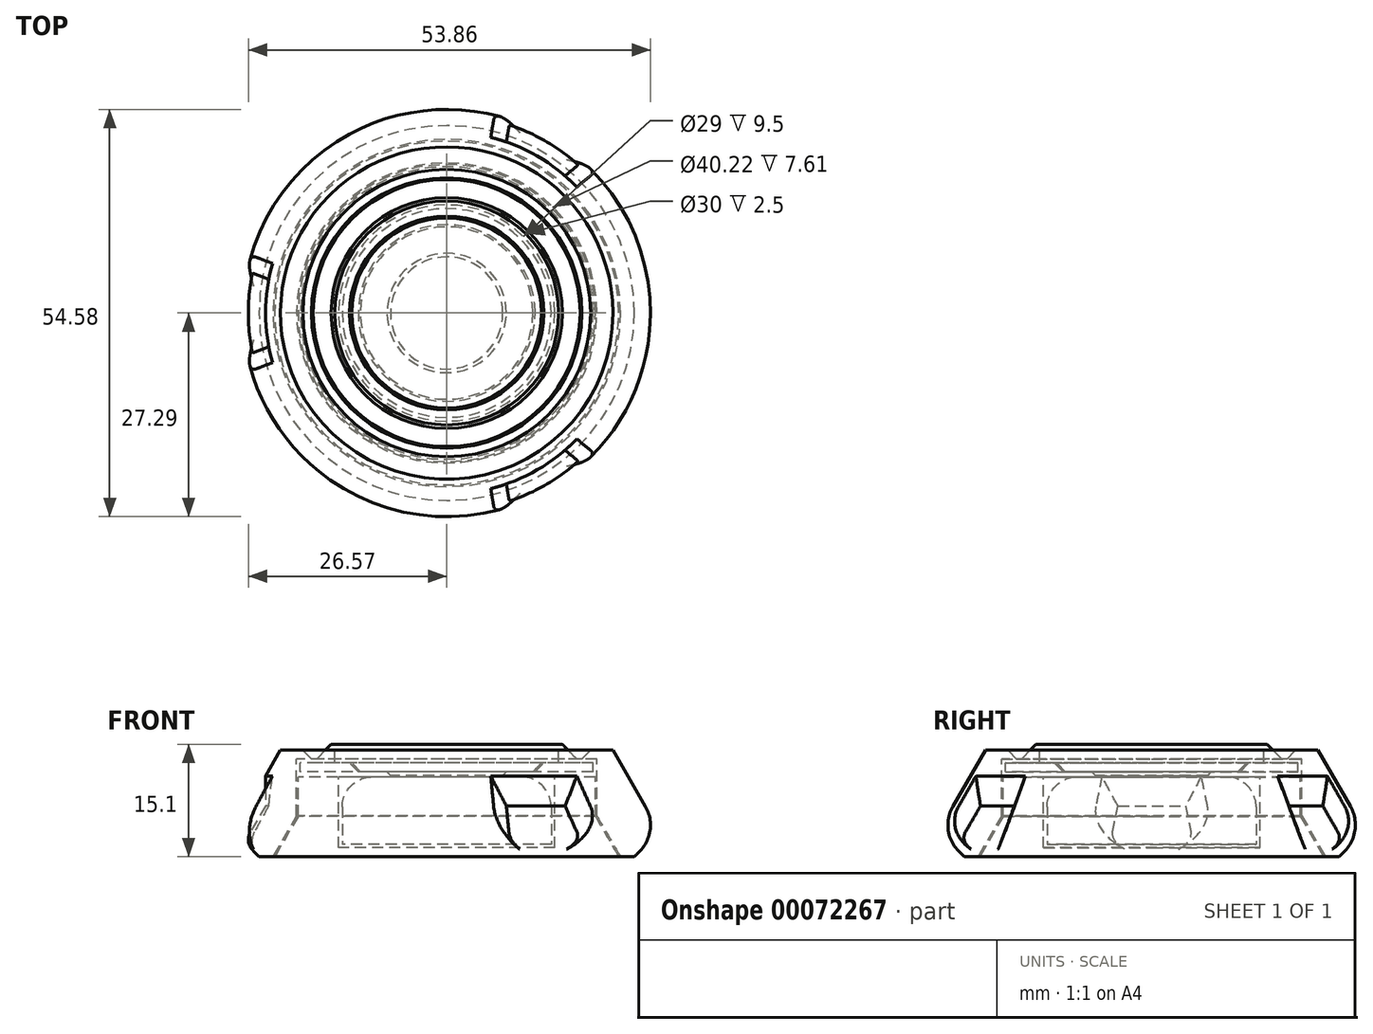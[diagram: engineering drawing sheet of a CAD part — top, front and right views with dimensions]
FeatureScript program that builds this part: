
annotation { "Feature Type Name" : "Feature", "Feature Type Description" : "" }
export const myFeature = defineFeature(function(context is Context, id is Id, definition is map)
    precondition{}
    {
        {
            var Q0;
            Q0=qCreatedBy(makeId("Top.planeOp"),FACE);
            var sketch = newSketch(context, id + "F0", { "sketchPlane" : qUnion([Q0])});
            skCircle(sketch, "E0", {"center": v(0, 0) * mm, "radius": 14 * mm});
            skSolve(sketch);
        }
        {
            var Q0;
            Q0=makeQuery(id+"F0.imprint","IMPRINT",FACE,{"disambiguationData":[TD([[makeQuery(id+"F0.imprint","IMPRINT",EDGE,{"derivedFrom":sQuery(id+"F0.wireOp",EDGE,"E0")}),1.0]])]});
            extrude(context, id + "F1", {"entities" : qUnion([Q0]), "depth" : 9 * mm});
        }
        {
            var Q0;
            Q0=makeQuery(id+"F1.opExtrude","CAP_EDGE",EDGE,{"disambiguationData":[OSD([sQuery(id+"F0.wireOp",EDGE,"E0")])],"isStart":false});
            fillet(context, id + "F2", {"entities" : qUnion([Q0]), "radius" : 4 * mm, "tangentPropagation" : true, "allowEdgeOverflow" : false});
        }
        {
            var Q0;
            Q0=qCreatedBy(makeId("Front.planeOp"),FACE);
            var sketch = newSketch(context, id + "F3", { "sketchPlane" : qUnion([Q0])});
            skLineSegment(sketch, "E1", {"start": v(-14.5, 9) * mm, "end": v(-14.5, -0.5) * mm});
            skLineSegment(sketch, "E2", {"start": v(-14.5, -0.5) * mm, "end": v(0, -0.5) * mm});
            skLineSegment(sketch, "E3", {"start": v(-14, 0) * mm, "end": v(-14, 5) * mm, "construction": true});
            skLineSegment(sketch, "E4", {"start": v(0, -0.5) * mm, "end": v(0, -1.7) * mm});
            skLineSegment(sketch, "E5", {"start": v(0, -1.7) * mm, "end": v(-23.05, -1.7) * mm});
            skLineSegment(sketch, "E6", {"start": v(-19.9, 3.74) * mm, "end": v(-19.9, 9) * mm});
            skLineSegment(sketch, "E7", {"start": v(-19.9, 9) * mm, "end": v(-14.5, 9) * mm});
            skLineSegment(sketch, "E8", {"start": v(-20.1, 3.8) * mm, "end": v(-20.1, 11.4) * mm});
            skLineSegment(sketch, "E9", {"start": v(-19.27, 12.6) * mm, "end": v(-18.1, 11.4) * mm});
            skLineSegment(sketch, "E10", {"start": v(-22.27, 12.6) * mm, "end": v(-30.52, -1.7) * mm});
            skLineSegment(sketch, "E11", {"start": v(-30.52, -1.7) * mm, "end": v(-23.28, -1.7) * mm});
            skLineSegment(sketch, "E12", {"start": v(-28.5, 1.8) * mm, "end": v(-25.13, -1.7) * mm});
            skLineSegment(sketch, "E13.bottom", {"start": v(0, 9.7) * mm, "end": v(-19.6, 9.7) * mm});
            skLineSegment(sketch, "E13.top", {"start": v(0, 10.9) * mm, "end": v(-19.6, 10.9) * mm});
            skLineSegment(sketch, "E13.left", {"start": v(0, 9.7) * mm, "end": v(0, 10.9) * mm});
            skLineSegment(sketch, "E14", {"start": v(-22.27, 12.6) * mm, "end": v(-19.27, 12.6) * mm});
            skLineSegment(sketch, "E15", {"start": v(-18.1, 11.4) * mm, "end": v(-20.1, 11.4) * mm});
            skLineSegment(sketch, "E16.bottom", {"start": v(0, 10.9) * mm, "end": v(-15, 10.9) * mm});
            skLineSegment(sketch, "E16.top", {"start": v(0, 13.9) * mm, "end": v(-15, 13.9) * mm, "construction": true});
            skLineSegment(sketch, "E16.left", {"start": v(0, 10.9) * mm, "end": v(0, 13.9) * mm});
            skLineSegment(sketch, "E16.right", {"start": v(-15, 10.9) * mm, "end": v(-15, 13.9) * mm});
            skLineSegment(sketch, "E17", {"start": v(0, 18.22) * mm, "end": v(0, 13.9) * mm});
            skLineSegment(sketch, "E18", {"start": v(-15, 13.9) * mm, "end": v(-17.9, 10.9) * mm});
            skLineSegment(sketch, "E19", {"start": v(-12.72, 10.9) * mm, "end": v(-11.56, 9.7) * mm});
            skLineSegment(sketch, "E20", {"start": v(-8, 9.7) * mm, "end": v(-8, 9.2) * mm});
            skLineSegment(sketch, "E21", {"start": v(-8, 9.2) * mm, "end": v(0, 9.2) * mm});
            skLineSegment(sketch, "E22", {"start": v(0, 9.2) * mm, "end": v(0, 9.7) * mm});
            skLineSegment(sketch, "E23", {"start": v(-13, 10.9) * mm, "end": v(-11.84, 9.7) * mm});
            skLineSegment(sketch, "E24", {"start": v(-15, 13.4) * mm, "end": v(-15.48, 13.4) * mm});
            skLineSegment(sketch, "E25", {"start": v(-8, 9.7) * mm, "end": v(-7.52, 9.2) * mm});
            skLineSegment(sketch, "E26", {"start": v(-27.06, 0.3) * mm, "end": v(-24.27, 5.14) * mm});
            skLineSegment(sketch, "E27", {"start": v(-24.27, 5.14) * mm, "end": v(-24.27, 9.14) * mm});
            skLineSegment(sketch, "E28", {"start": v(-19.6, 10.9) * mm, "end": v(-19.6, 9.7) * mm});
            skLineSegment(sketch, "E29", {"start": v(-20.1, 3.8) * mm, "end": v(-23.28, -1.7) * mm});
            skLineSegment(sketch, "E30", {"start": v(-19.9, 3.74) * mm, "end": v(-23.05, -1.7) * mm});
            skSolve(sketch);
        }
        {
            var Q0;
            {var subQ5=sQuery(id+"F3.wireOp",EDGE,"E24");Q0=makeQuery(id+"F3.imprint","IMPRINT",FACE,{"disambiguationData":[TD([[makeQuery(id+"F3.imprint","IMPRINT",EDGE,{"derivedFrom":subQ5}),1.0]])]});}
            var Q1;
            {var subQ5=sQuery(id+"F3.wireOp",EDGE,"E23");Q1=makeQuery(id+"F3.imprint","IMPRINT",FACE,{"disambiguationData":[TD([[makeQuery(id+"F3.imprint","IMPRINT",EDGE,{"derivedFrom":subQ5}),-1.0]])]});}
            var Q2;
            {var subQ0=sQuery(id+"F3.wireOp",EDGE,"E13.left");Q2=makeQuery(id+"F3.imprint","IMPRINT",FACE,{"disambiguationData":[TD([[makeQuery(id+"F3.imprint","IMPRINT",EDGE,{"derivedFrom":subQ0}),1.0]])]});}
            var Q3;
            {var subQ0=sQuery(id+"F3.wireOp",EDGE,"E22");Q3=makeQuery(id+"F3.imprint","IMPRINT",FACE,{"disambiguationData":[TD([[makeQuery(id+"F3.imprint","IMPRINT",EDGE,{"derivedFrom":subQ0}),1.0]])]});}
            var Q4;
            Q4=makeQuery(id+"F3.imprint","IMPRINT",FACE,{"disambiguationData":[TD([[makeQuery(id+"F3.imprint","IMPRINT",EDGE,{"derivedFrom":sQuery(id+"F3.wireOp",EDGE,"E8")}),1.0]])]});
            var Q5;
            Q5=makeQuery(id+"F3.imprint","IMPRINT",FACE,{"disambiguationData":[TD([[makeQuery(id+"F3.imprint","IMPRINT",EDGE,{"derivedFrom":sQuery(id+"F3.wireOp",EDGE,"E1")}),-1.0]])]});
            var Q6;
            {var subQ4=sQuery(id+"F3.wireOp",EDGE,"ZmY2TIqv-RjT7-Huph-ke3o-9Fy59m0xxHUF");Q6=makeQuery(id+"F3.imprint","IMPRINT",FACE,{"disambiguationData":[TD([[makeQuery(id+"F3.imprint","IMPRINT",EDGE,{"derivedFrom":subQ4}),-1.0]])]});}
            var Q7;
            {var subQ4=sQuery(id+"F3.wireOp",EDGE,"E26");Q7=makeQuery(id+"F3.imprint","IMPRINT",FACE,{"disambiguationData":[TD([[makeQuery(id+"F3.imprint","IMPRINT",EDGE,{"derivedFrom":subQ4}),1.0]])]});}
            var Q8;
            Q8=sQuery(id+"F3.wireOp",EDGE,"E17");
            revolve(context, id + "F4", {"entities" : qUnion([Q0, Q1, Q2, Q3, Q4, Q5, Q6, Q7]), "axis" : qUnion([Q8]), "revolveType" : RevolveType.FULL});
        }
        {
            var Q0;
            Q0=makeQuery(id+"F4.opRevolve","SWEPT_EDGE",EDGE,{"disambiguationData":[OSD([sQuery(id+"F3.wireOp",EDGE,"E10"),sQuery(id+"F3.wireOp",EDGE,"E12")])]});
            fillet(context, id + "F5", {"entities" : qUnion([Q0]), "radius" : 5 * mm, "tangentPropagation" : true, "allowEdgeOverflow" : false});
        }
        {
            var Q0;
            {var subQ4=sQuery(id+"F3.wireOp",EDGE,"E26");Q0=makeQuery(id+"F3.imprint","IMPRINT",FACE,{"disambiguationData":[TD([[makeQuery(id+"F3.imprint","IMPRINT",EDGE,{"derivedFrom":subQ4}),1.0]])]});}
            var Q1;
            Q1=sQuery(id+"F3.wireOp",EDGE,"E17");
            revolve(context, id + "F6", {"operationType" : NewBodyOperationType.REMOVE, "entities" : qUnion([Q0]), "axis" : qUnion([Q1]), "revolveType" : RevolveType.SYMMETRIC, "oppositeDirection" : true, "angle" : 45 * degree});
        }
        {
            var Q0;
            Q0=makeQuery(id+"F6.boolean.opBoolean","COPY",EDGE,{"derivedFrom":makeQuery(id+"F6.opRevolve","CAP_EDGE",EDGE,{"disambiguationData":[OSD([sQuery(id+"F3.wireOp",EDGE,"E26")])],"isStart":true})});
            var Q1;
            Q1=makeQuery(id+"F6.boolean.opBoolean","COPY",EDGE,{"derivedFrom":makeQuery(id+"F6.opRevolve","CAP_EDGE",EDGE,{"disambiguationData":[OSD([sQuery(id+"F3.wireOp",EDGE,"E26")])],"isStart":false})});
            chamfer(context, id + "F7", {"entities" : qUnion([Q0, Q1]), "width" : 5 * mm, "tangentPropagation" : true});
        }
        {
            var Q0;
            Q0=makeQuery(id+"F4.opRevolve","SWEPT_BODY",BODY,{"disambiguationData":[OSD([sQuery(id+"F3.wireOp",EDGE,"E8"),sQuery(id+"F3.wireOp",EDGE,"sHKzPFwf-f77H-S0fX-YXo6-HXbzY9a9a5wL"),sQuery(id+"F3.wireOp",EDGE,"E9"),sQuery(id+"F3.wireOp",EDGE,"E10"),sQuery(id+"F3.wireOp",EDGE,"E11"),sQuery(id+"F3.wireOp",EDGE,"E12"),sQuery(id+"F3.wireOp",EDGE,"E14"),sQuery(id+"F3.wireOp",EDGE,"E15")])]});
            var Q1;
            {var subQ0=sQuery(id+"F3.wireOp",EDGE,"E26");Q1=makeQuery(id+"F7.opChamfer","BLEND_FACE",FACE,{"disambiguationData":[OSD([subQ0]),TDD([makeQuery(id+"F6.boolean.opBoolean","COPY",EDGE,{"derivedFrom":makeQuery(id+"F6.opRevolve","CAP_EDGE",EDGE,{"disambiguationData":[OSD([subQ0])],"isStart":true})})])]});}
            var Q2;
            Q2=makeQuery(id+"F6.boolean.opBoolean","COPY",FACE,{"derivedFrom":makeQuery(id+"F6.opRevolve","SWEPT_FACE",FACE,{"disambiguationData":[OSD([sQuery(id+"F3.wireOp",EDGE,"E27")])]})});
            var Q3;
            Q3=makeQuery(id+"F6.boolean.opBoolean","COPY",FACE,{"derivedFrom":makeQuery(id+"F6.opRevolve","SWEPT_FACE",FACE,{"disambiguationData":[OSD([sQuery(id+"F3.wireOp",EDGE,"E26")])]})});
            var Q4;
            {var subQ0=sQuery(id+"F3.wireOp",EDGE,"E26");Q4=makeQuery(id+"F7.opChamfer","BLEND_FACE",FACE,{"disambiguationData":[OSD([subQ0]),TDD([makeQuery(id+"F6.boolean.opBoolean","COPY",EDGE,{"derivedFrom":makeQuery(id+"F6.opRevolve","CAP_EDGE",EDGE,{"disambiguationData":[OSD([subQ0])],"isStart":false})})])]});}
            var Q5;
            Q5=makeQuery(id+"F4.opRevolve","SWEPT_EDGE",EDGE,{"disambiguationData":[OSD([sQuery(id+"F3.wireOp",EDGE,"ZmY2TIqv-RjT7-Huph-ke3o-9Fy59m0xxHUF"),sQuery(id+"F3.wireOp",EDGE,"E10"),sQuery(id+"F3.wireOp",EDGE,"E14")])]});
            circularPattern(context, id + "F8", {"faces" : qUnion([Q1, Q2, Q3, Q4]), "axis" : qUnion([Q5]), "angle" : 120 * degree, "instanceCount" : round(3), "patternType" : PatternType.FACE, "computeTransformsWithoutBuiltin" : true});
        }
        {
            var Q0;
            Q0=makeQuery(id+"F6.boolean.opBoolean","INTERSECT",EDGE,{"derivedFrom":[makeQuery(id+"F5.opFillet","BLEND_FACE",FACE,{"disambiguationData":[OSD([sQuery(id+"F3.wireOp",EDGE,"E10"),sQuery(id+"F3.wireOp",EDGE,"E12")])]}),makeQuery(id+"F6.opRevolve","SWEPT_FACE",FACE,{"disambiguationData":[OSD([sQuery(id+"F3.wireOp",EDGE,"E26")])]})]});
            var Q1;
            Q1=makeQuery(id+"F8.opPattern","COPY",EDGE,{"derivedFrom":makeQuery(id+"F6.boolean.opBoolean","INTERSECT",EDGE,{"derivedFrom":[makeQuery(id+"F5.opFillet","BLEND_FACE",FACE,{"disambiguationData":[OSD([sQuery(id+"F3.wireOp",EDGE,"E10"),sQuery(id+"F3.wireOp",EDGE,"E12")])]}),makeQuery(id+"F6.opRevolve","SWEPT_FACE",FACE,{"disambiguationData":[OSD([sQuery(id+"F3.wireOp",EDGE,"E26")])]})]}),"instanceName":"1"});
            var Q2;
            Q2=makeQuery(id+"F8.opPattern","COPY",EDGE,{"derivedFrom":makeQuery(id+"F6.boolean.opBoolean","INTERSECT",EDGE,{"derivedFrom":[makeQuery(id+"F5.opFillet","BLEND_FACE",FACE,{"disambiguationData":[OSD([sQuery(id+"F3.wireOp",EDGE,"E10"),sQuery(id+"F3.wireOp",EDGE,"E12")])]}),makeQuery(id+"F6.opRevolve","SWEPT_FACE",FACE,{"disambiguationData":[OSD([sQuery(id+"F3.wireOp",EDGE,"E26")])]})]}),"instanceName":"2"});
            fillet(context, id + "F9", {"entities" : qUnion([Q0, Q1, Q2]), "radius" : 2 * mm, "tangentPropagation" : true, "allowEdgeOverflow" : false});
        }
    });
